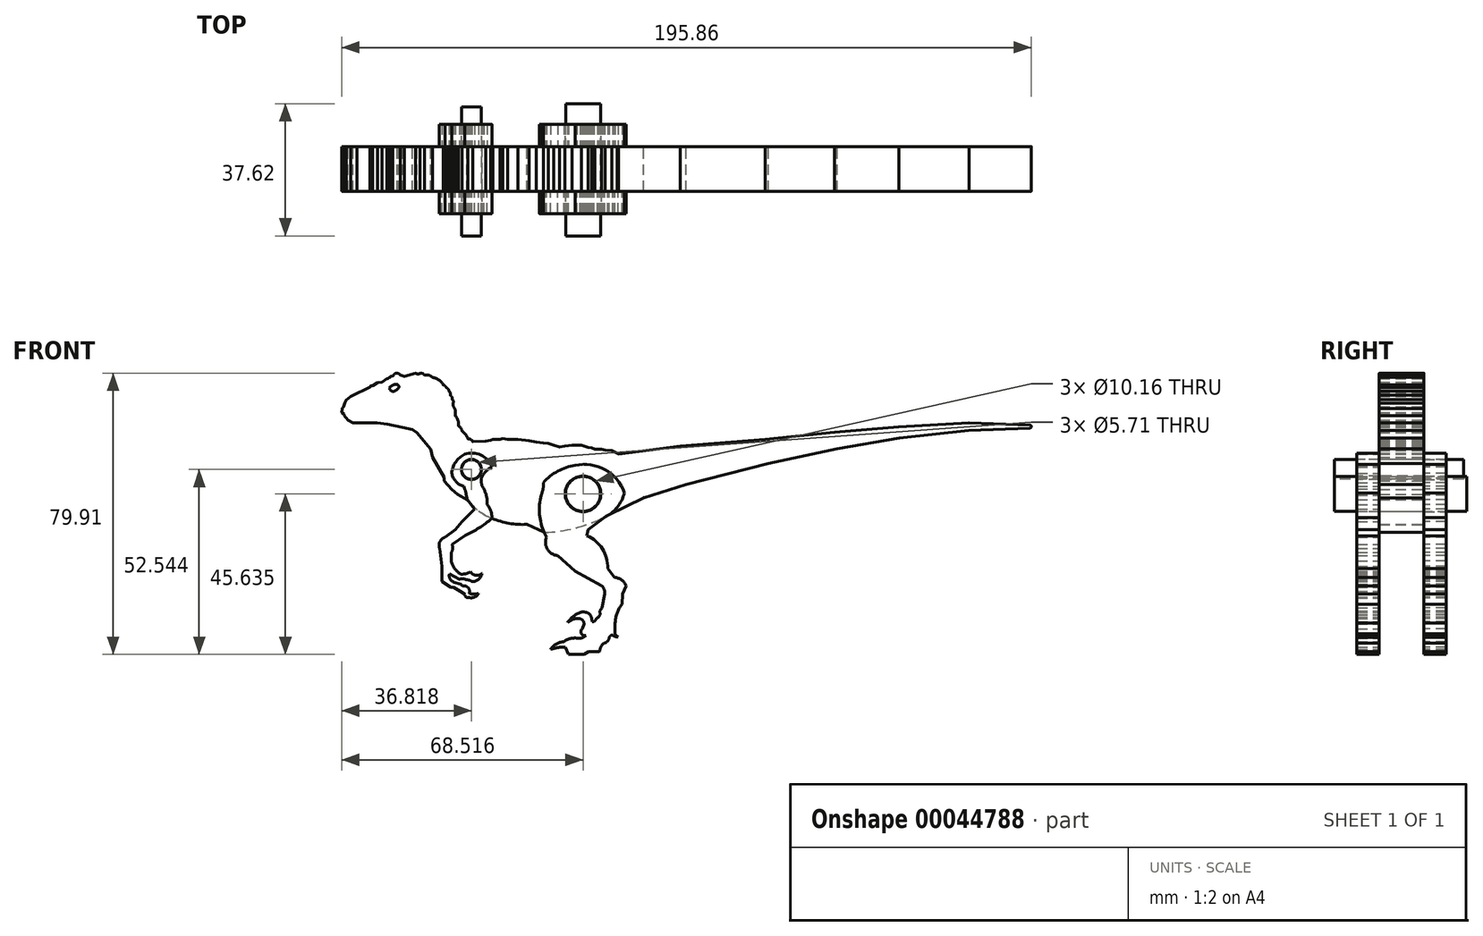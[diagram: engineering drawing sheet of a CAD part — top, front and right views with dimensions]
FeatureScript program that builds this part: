
annotation { "Feature Type Name" : "Feature", "Feature Type Description" : "" }
export const myFeature = defineFeature(function(context is Context, id is Id, definition is map)
    precondition{}
    {
        {
            var Q0;
            Q0=qCreatedBy(makeId("Front.planeOp"),FACE);
            var sketch = newSketch(context, id + "F0", { "sketchPlane" : qUnion([Q0])});
            skLineSegment(sketch, "E0", {"start": v(-125.93, 65.9) * mm, "end": v(-108.35, 68.14) * mm});
            skLineSegment(sketch, "E1", {"start": v(-108.35, 68.14) * mm, "end": v(-84.22, 70.03) * mm});
            skLineSegment(sketch, "E2", {"start": v(-84.22, 70.03) * mm, "end": v(-64.57, 72.1) * mm});
            skLineSegment(sketch, "E3", {"start": v(-64.57, 72.1) * mm, "end": v(-46.3, 73.65) * mm});
            skLineSegment(sketch, "E4", {"start": v(-46.3, 73.65) * mm, "end": v(-26.38, 74.75) * mm});
            skLineSegment(sketch, "E5", {"start": v(-26.38, 74.75) * mm, "end": v(-9.06, 74.08) * mm});
            skArc(sketch, "E6", {"start": v(-9.06, 73.26) * mm, "mid": v(-8.66, 73.67) * mm, "end": v(-9.06, 74.08) * mm});
            skLineSegment(sketch, "E7", {"start": v(-9.06, 73.26) * mm, "end": v(-26.44, 72.6) * mm});
            skLineSegment(sketch, "E8", {"start": v(-26.44, 72.6) * mm, "end": v(-46.15, 70.45) * mm});
            skLineSegment(sketch, "E9", {"start": v(-46.15, 70.45) * mm, "end": v(-63.78, 67.32) * mm});
            skLineSegment(sketch, "E10", {"start": v(-63.78, 67.32) * mm, "end": v(-83.4, 63.22) * mm});
            skLineSegment(sketch, "E11", {"start": v(-83.4, 63.22) * mm, "end": v(-106.71, 57.18) * mm});
            skLineSegment(sketch, "E12", {"start": v(-106.71, 57.18) * mm, "end": v(-118.86, 53.44) * mm});
            skLineSegment(sketch, "E13", {"start": v(-118.86, 53.44) * mm, "end": v(-130.03, 47.9) * mm});
            skPoint(sketch, "E14.endSnap0", {"position": v(-132.94, 9.77) * mm});
            skLineSegment(sketch, "E15", {"start": v(-147.05, 43.57) * mm, "end": v(-151.91, 45.87) * mm});
            skArc(sketch, "E16", {"start": v(-161.96, 47.61) * mm, "mid": v(-157.04, 46.17) * mm, "end": v(-151.91, 45.87) * mm});
            skLineSegment(sketch, "E17", {"start": v(-168.99, 52.93) * mm, "end": v(-171.65, 54.46) * mm});
            skLineSegment(sketch, "E18", {"start": v(-171.65, 54.46) * mm, "end": v(-173.34, 55.8) * mm});
            skLineSegment(sketch, "E19", {"start": v(-173.34, 55.8) * mm, "end": v(-175.45, 58.25) * mm});
            skLineSegment(sketch, "E20", {"start": v(-175.45, 58.25) * mm, "end": v(-175.47, 59.23) * mm});
            skLineSegment(sketch, "E21", {"start": v(-175.47, 59.23) * mm, "end": v(-177.78, 63.2) * mm});
            skLineSegment(sketch, "E22", {"start": v(-177.78, 63.2) * mm, "end": v(-178.8, 64.97) * mm});
            skLineSegment(sketch, "E23", {"start": v(-178.8, 64.97) * mm, "end": v(-179.31, 67.25) * mm});
            skLineSegment(sketch, "E24", {"start": v(-179.31, 67.25) * mm, "end": v(-183.18, 71.9) * mm});
            skLineSegment(sketch, "E25", {"start": v(-183.18, 71.9) * mm, "end": v(-184.49, 72.8) * mm});
            skLineSegment(sketch, "E26", {"start": v(-184.49, 72.8) * mm, "end": v(-187.38, 73.5) * mm});
            skLineSegment(sketch, "E27", {"start": v(-187.38, 73.5) * mm, "end": v(-189.84, 74) * mm});
            skLineSegment(sketch, "E28", {"start": v(-189.84, 74) * mm, "end": v(-191.62, 74.38) * mm});
            skLineSegment(sketch, "E29", {"start": v(-191.62, 74.38) * mm, "end": v(-194.53, 74.67) * mm});
            skLineSegment(sketch, "E30", {"start": v(-194.53, 74.67) * mm, "end": v(-197.25, 74.67) * mm});
            skLineSegment(sketch, "E31", {"start": v(-197.25, 74.67) * mm, "end": v(-200.12, 74.67) * mm});
            skLineSegment(sketch, "E32", {"start": v(-200.12, 74.67) * mm, "end": v(-201.34, 74.67) * mm});
            skLineSegment(sketch, "E33", {"start": v(-201.34, 74.67) * mm, "end": v(-202.78, 75.5) * mm});
            skLineSegment(sketch, "E34", {"start": v(-202.78, 75.5) * mm, "end": v(-203.96, 76.93) * mm});
            skLineSegment(sketch, "E35", {"start": v(-203.96, 77.29) * mm, "end": v(-204.52, 77.65) * mm});
            skLineSegment(sketch, "E36", {"start": v(-204.52, 77.65) * mm, "end": v(-204.44, 78.8) * mm});
            skLineSegment(sketch, "E37", {"start": v(-204.44, 78.8) * mm, "end": v(-204.09, 79.26) * mm});
            skLineSegment(sketch, "E38", {"start": v(-204.09, 79.26) * mm, "end": v(-203.68, 80.39) * mm});
            skLineSegment(sketch, "E39", {"start": v(-203.68, 80.39) * mm, "end": v(-203.32, 81.16) * mm});
            skLineSegment(sketch, "E40", {"start": v(-203.32, 81.16) * mm, "end": v(-201.99, 82.18) * mm});
            skLineSegment(sketch, "E41", {"start": v(-201.99, 82.18) * mm, "end": v(-200.22, 83.1) * mm});
            skLineSegment(sketch, "E42", {"start": v(-200.22, 83.1) * mm, "end": v(-198.01, 84.18) * mm});
            skLineSegment(sketch, "E43", {"start": v(-198.01, 84.18) * mm, "end": v(-196.55, 84.9) * mm});
            skLineSegment(sketch, "E44", {"start": v(-196.55, 84.9) * mm, "end": v(-196.3, 85.25) * mm});
            skLineSegment(sketch, "E45", {"start": v(-196.3, 85.25) * mm, "end": v(-195.76, 85.33) * mm});
            skLineSegment(sketch, "E46", {"start": v(-195.76, 85.33) * mm, "end": v(-194.43, 86.15) * mm});
            skLineSegment(sketch, "E47", {"start": v(-194.43, 86.15) * mm, "end": v(-193.15, 86.23) * mm});
            skLineSegment(sketch, "E48", {"start": v(-193.15, 86.23) * mm, "end": v(-191.76, 87.3) * mm});
            skLineSegment(sketch, "E49", {"start": v(-191.76, 87.3) * mm, "end": v(-191.4, 87.3) * mm});
            skLineSegment(sketch, "E50", {"start": v(-191.4, 87.3) * mm, "end": v(-191, 87.69) * mm});
            skLineSegment(sketch, "E51", {"start": v(-191, 87.69) * mm, "end": v(-190.82, 87.69) * mm});
            skLineSegment(sketch, "E52", {"start": v(-190.82, 87.69) * mm, "end": v(-190.53, 87.94) * mm});
            skLineSegment(sketch, "E53", {"start": v(-190.53, 87.94) * mm, "end": v(-190, 88.02) * mm});
            skArc(sketch, "E54", {"start": v(-187.95, 88.35) * mm, "mid": v(-189.08, 88.84) * mm, "end": v(-190, 88.02) * mm});
            skLineSegment(sketch, "E55", {"start": v(-187.95, 88.35) * mm, "end": v(-186.77, 87.92) * mm});
            skLineSegment(sketch, "E56", {"start": v(-186.77, 87.92) * mm, "end": v(-183.56, 88.85) * mm});
            skArc(sketch, "E57", {"start": v(-183.56, 88.85) * mm, "mid": v(-182.98, 88.62) * mm, "end": v(-182.36, 88.76) * mm});
            skArc(sketch, "E58", {"start": v(-180.98, 88.3) * mm, "mid": v(-181.6, 88.76) * mm, "end": v(-182.36, 88.76) * mm});
            skArc(sketch, "E59", {"start": v(-178.74, 87.64) * mm, "mid": v(-179.77, 88.28) * mm, "end": v(-180.98, 88.3) * mm});
            skArc(sketch, "E60", {"start": v(-175.7, 85.54) * mm, "mid": v(-176.97, 86.96) * mm, "end": v(-178.74, 87.64) * mm});
            skArc(sketch, "E61", {"start": v(-174.82, 84.77) * mm, "mid": v(-175.2, 85.23) * mm, "end": v(-175.7, 85.54) * mm});
            skArc(sketch, "E62", {"start": v(-174.03, 83.74) * mm, "mid": v(-174.33, 84.33) * mm, "end": v(-174.82, 84.77) * mm});
            skArc(sketch, "E63", {"start": v(-173.68, 82.56) * mm, "mid": v(-173.72, 83.2) * mm, "end": v(-174.03, 83.74) * mm});
            skArc(sketch, "E64", {"start": v(-173.11, 81.35) * mm, "mid": v(-173.23, 82.04) * mm, "end": v(-173.68, 82.56) * mm});
            skArc(sketch, "E65", {"start": v(-172.9, 80.34) * mm, "mid": v(-172.83, 80.88) * mm, "end": v(-173.11, 81.35) * mm});
            skArc(sketch, "E66", {"start": v(-172.9, 80.34) * mm, "mid": v(-172.83, 79.49) * mm, "end": v(-172.42, 78.74) * mm});
            skArc(sketch, "E67", {"start": v(-172.28, 76.73) * mm, "mid": v(-172.22, 77.74) * mm, "end": v(-172.42, 78.74) * mm});
            skArc(sketch, "E68", {"start": v(-171.43, 73.91) * mm, "mid": v(-171.52, 75.42) * mm, "end": v(-172.28, 76.73) * mm});
            skArc(sketch, "E69", {"start": v(-170.37, 72.43) * mm, "mid": v(-170.75, 73.28) * mm, "end": v(-171.43, 73.91) * mm});
            skArc(sketch, "E70", {"start": v(-168.66, 70.2) * mm, "mid": v(-169.34, 71.45) * mm, "end": v(-170.37, 72.43) * mm});
            skArc(sketch, "E71", {"start": v(-167.32, 69.36) * mm, "mid": v(-167.86, 69.98) * mm, "end": v(-168.66, 70.2) * mm});
            skLineSegment(sketch, "E72", {"start": v(-167.32, 69.36) * mm, "end": v(-163.58, 69.58) * mm});
            skLineSegment(sketch, "E73", {"start": v(-163.58, 69.58) * mm, "end": v(-162.22, 69.8) * mm});
            skLineSegment(sketch, "E74", {"start": v(-162.22, 69.8) * mm, "end": v(-161.63, 70.06) * mm});
            skLineSegment(sketch, "E75", {"start": v(-161.63, 70.06) * mm, "end": v(-159.56, 70.09) * mm});
            skLineSegment(sketch, "E76", {"start": v(-159.56, 70.09) * mm, "end": v(-158.84, 70.24) * mm});
            skLineSegment(sketch, "E77", {"start": v(-158.84, 70.24) * mm, "end": v(-157.36, 70.06) * mm});
            skLineSegment(sketch, "E78", {"start": v(-157.36, 70.06) * mm, "end": v(-154.44, 70.01) * mm});
            skLineSegment(sketch, "E79", {"start": v(-154.44, 70.01) * mm, "end": v(-151.36, 69.68) * mm});
            skLineSegment(sketch, "E80", {"start": v(-151.36, 69.68) * mm, "end": v(-149.29, 69.27) * mm});
            skLineSegment(sketch, "E81", {"start": v(-149.29, 69.27) * mm, "end": v(-147.29, 69.04) * mm});
            skLineSegment(sketch, "E82", {"start": v(-147.29, 69.04) * mm, "end": v(-145.8, 68.94) * mm});
            skLineSegment(sketch, "E83", {"start": v(-145.8, 68.94) * mm, "end": v(-144.37, 68.37) * mm});
            skLineSegment(sketch, "E84", {"start": v(-144.37, 68.37) * mm, "end": v(-142.63, 67.91) * mm});
            skLineSegment(sketch, "E85", {"start": v(-142.63, 67.91) * mm, "end": v(-141.22, 68.14) * mm});
            skLineSegment(sketch, "E86", {"start": v(-141.22, 68.14) * mm, "end": v(-139.12, 68.32) * mm});
            skLineSegment(sketch, "E87", {"start": v(-139.12, 68.32) * mm, "end": v(-136.45, 68.32) * mm});
            skLineSegment(sketch, "E88", {"start": v(-136.45, 68.32) * mm, "end": v(-134.56, 67.8) * mm});
            skLineSegment(sketch, "E89", {"start": v(-134.56, 67.8) * mm, "end": v(-133.53, 67.68) * mm});
            skLineSegment(sketch, "E90", {"start": v(-133.53, 67.68) * mm, "end": v(-132.64, 67.3) * mm});
            skLineSegment(sketch, "E91", {"start": v(-132.64, 67.3) * mm, "end": v(-130.69, 67.27) * mm});
            skLineSegment(sketch, "E92", {"start": v(-130.69, 67.27) * mm, "end": v(-129.66, 66.99) * mm});
            skLineSegment(sketch, "E93", {"start": v(-129.66, 66.99) * mm, "end": v(-127.82, 66.86) * mm});
            skLineSegment(sketch, "E94", {"start": v(-127.82, 66.86) * mm, "end": v(-126.26, 66.12) * mm});
            skLineSegment(sketch, "E95", {"start": v(-126.26, 66.12) * mm, "end": v(-125.93, 65.9) * mm});
            skArc(sketch, "E96", {"start": v(-188.76, 85.67) * mm, "mid": v(-190.05, 85.46) * mm, "end": v(-191.02, 84.58) * mm});
            skArc(sketch, "E97", {"start": v(-188.28, 84.82) * mm, "mid": v(-188.41, 85.3) * mm, "end": v(-188.76, 85.67) * mm});
            skArc(sketch, "E98", {"start": v(-189.83, 83.66) * mm, "mid": v(-188.94, 84.09) * mm, "end": v(-188.28, 84.82) * mm});
            skArc(sketch, "E99", {"start": v(-191.02, 84.58) * mm, "mid": v(-190.58, 83.92) * mm, "end": v(-189.83, 83.66) * mm});
            skLineSegment(sketch, "E100", {"start": v(-194.53, 74.67) * mm, "end": v(-187.58, 74.67) * mm});
            skArc(sketch, "E101", {"start": v(-187.58, 74.67) * mm, "mid": v(-186.04, 74.88) * mm, "end": v(-184.6, 75.5) * mm});
            skArc(sketch, "E102", {"start": v(-184.6, 75.5) * mm, "mid": v(-183.22, 76.44) * mm, "end": v(-182.32, 77.85) * mm});
            skArc(sketch, "E103", {"start": v(-181.83, 79.96) * mm, "mid": v(-182.4, 78.98) * mm, "end": v(-182.32, 77.85) * mm});
            skLineSegment(sketch, "E104", {"start": v(-203.96, 77.29) * mm, "end": v(-203.96, 76.93) * mm});
            skArc(sketch, "E105", {"start": v(-168.99, 52.93) * mm, "mid": v(-165.8, 49.85) * mm, "end": v(-161.96, 47.61) * mm});
            skPoint(sketch, "E106.end.orphan", {"position": v(-173.5, 37.9) * mm});
            skPoint(sketch, "E107.end.orphan", {"position": v(-165.75, 26.36) * mm});
            skPoint(sketch, "E108.start.orphan", {"position": v(-168.42, 26.36) * mm});
            skPoint(sketch, "E109.center.orphan", {"position": v(-167.5, 32.44) * mm});
            skPoint(sketch, "E110.end.orphan", {"position": v(-168.04, 32.44) * mm});
            skPoint(sketch, "E111.start.orphan", {"position": v(-173.5, 35.58) * mm});
            skArc(sketch, "E112", {"start": v(-147.05, 43.57) * mm, "mid": v(-138.3, 44.84) * mm, "end": v(-130.03, 47.9) * mm});
            skPoint(sketch, "E113.orphan", {"position": v(-131.41, 9.77) * mm});
            skPoint(sketch, "E114.start.orphan", {"position": v(-134.46, 9.77) * mm});
            skPoint(sketch, "E14.end.orphan", {"position": v(-132.94, 18.26) * mm});
            skSolve(sketch);
        }
        {
            var Q0;
            Q0 = qSketchRegion(id + "F0", true);
            extrude(context, id + "F1", {"entities" : qUnion([Q0]), "depth" : 12.7 * mm});
        }
        {
            var Q0;
            Q0=makeQuery(id+"F1.opExtrude","CAP_FACE",FACE,{"disambiguationData":[OSD([sQuery(id+"F0.wireOp",EDGE,"E0"),sQuery(id+"F0.wireOp",EDGE,"E1"),sQuery(id+"F0.wireOp",EDGE,"E2"),sQuery(id+"F0.wireOp",EDGE,"E3"),sQuery(id+"F0.wireOp",EDGE,"E4"),sQuery(id+"F0.wireOp",EDGE,"E5"),sQuery(id+"F0.wireOp",EDGE,"E6"),sQuery(id+"F0.wireOp",EDGE,"E7"),sQuery(id+"F0.wireOp",EDGE,"E8"),sQuery(id+"F0.wireOp",EDGE,"E9"),sQuery(id+"F0.wireOp",EDGE,"E10"),sQuery(id+"F0.wireOp",EDGE,"E11"),sQuery(id+"F0.wireOp",EDGE,"E12"),sQuery(id+"F0.wireOp",EDGE,"E13"),sQuery(id+"F0.wireOp",EDGE,"24e5a3a4-4c74-4cf4-83a0-4dd23b862dd2"),sQuery(id+"F0.wireOp",EDGE,"080116d6-97e3-4202-9e88-d1089f754f1b"),sQuery(id+"F0.wireOp",EDGE,"d3884d33-9078-405f-b6df-4c04f3e83864"),sQuery(id+"F0.wireOp",EDGE,"febd36f7-1211-4430-a0e6-d8187a314ec4"),sQuery(id+"F0.wireOp",EDGE,"da5aa56b-a51a-4f41-be61-5bd352a00608"),sQuery(id+"F0.wireOp",EDGE,"d6cba1f3-012b-44de-a797-d860b0189383"),sQuery(id+"F0.wireOp",EDGE,"37a4c888-297b-4a02-801f-539c14ebc06d"),sQuery(id+"F0.wireOp",EDGE,"e4f4d76b-1661-4bd5-9ee1-3f521e7b8a22"),sQuery(id+"F0.wireOp",EDGE,"979e7fdc-73c7-4f33-a677-fdc23efbcfdc"),sQuery(id+"F0.wireOp",EDGE,"29fca69b-b50e-4ce2-ab5e-5b8caaeedcb0"),sQuery(id+"F0.wireOp",EDGE,"8e0e4076-9d8e-4c43-9cb5-455944ac78b8"),sQuery(id+"F0.wireOp",EDGE,"44bc8136-e123-4d3f-885e-bba49d30737f"),sQuery(id+"F0.wireOp",EDGE,"525c7c83-05e1-4472-ad50-cb793b361226"),sQuery(id+"F0.wireOp",EDGE,"5d251ab0-8bdf-4815-aee8-ee65ace502ef"),sQuery(id+"F0.wireOp",EDGE,"27625abd-22d6-4f79-a906-6ae342303200"),sQuery(id+"F0.wireOp",EDGE,"E114"),sQuery(id+"F0.wireOp",EDGE,"e7f71301-65a4-4f7e-82f1-78113fcac0ca"),sQuery(id+"F0.wireOp",EDGE,"26476aea-994e-4d0f-ac5c-cd76c3ac9e5d"),sQuery(id+"F0.wireOp",EDGE,"03a9189d-c466-419f-af76-e664bc940cea"),sQuery(id+"F0.wireOp",EDGE,"69aa97cf-a6f8-4194-888d-ef945e605e21"),sQuery(id+"F0.wireOp",EDGE,"afc6dbb8-0825-4bc3-9a9d-32ddbc67a7fa"),sQuery(id+"F0.wireOp",EDGE,"0628672f-60e4-485e-babd-115e9d53bd91"),sQuery(id+"F0.wireOp",EDGE,"e0d62bde-7324-42d2-bb55-b3d343f8089d"),sQuery(id+"F0.wireOp",EDGE,"1e4123c9-30b8-4527-b1a6-3343e65eabf4"),sQuery(id+"F0.wireOp",EDGE,"09e39b06-8005-44ff-a5a9-aa5534c9f029"),sQuery(id+"F0.wireOp",EDGE,"23136ab9-187e-40da-8f19-5e2a66e5e931"),sQuery(id+"F0.wireOp",EDGE,"bbcf107a-c80a-4753-81d0-061c0fd05650"),sQuery(id+"F0.wireOp",EDGE,"cf572bc4-ae00-43a8-be20-ca718d7e2706"),sQuery(id+"F0.wireOp",EDGE,"2e92d61d-f502-4e42-9fb1-9756a9c91f70"),sQuery(id+"F0.wireOp",EDGE,"E14"),sQuery(id+"F0.wireOp",EDGE,"ce39f346-d287-4330-8f07-a5cfedcd8c1d"),sQuery(id+"F0.wireOp",EDGE,"58f72196-1935-4dd5-9193-2e0d50fd29e6"),sQuery(id+"F0.wireOp",EDGE,"e48e3e90-8ca5-40ff-9788-39b801b58fd2"),sQuery(id+"F0.wireOp",EDGE,"65447df7-b8a0-446b-9d25-0bb36401ba05"),sQuery(id+"F0.wireOp",EDGE,"5d1346c8-a41c-40e0-b5fa-ddddd0b284a1"),sQuery(id+"F0.wireOp",EDGE,"65ad6121-d8a3-40ab-a185-4ab3d7fadf29"),sQuery(id+"F0.wireOp",EDGE,"d791e0c2-2edb-42dd-ace2-d81078d97bde"),sQuery(id+"F0.wireOp",EDGE,"d9b75e36-ac99-4c51-9c33-fa74f8d5a9b3"),sQuery(id+"F0.wireOp",EDGE,"03808c8b-abac-4ab2-9cbf-64fa338352f3"),sQuery(id+"F0.wireOp",EDGE,"88808034-b678-4790-916c-13f8a42bf5bf"),sQuery(id+"F0.wireOp",EDGE,"87ca94a4-f72d-4e60-8cfd-468d838f297d"),sQuery(id+"F0.wireOp",EDGE,"E15"),sQuery(id+"F0.wireOp",EDGE,"E16"),sQuery(id+"F0.wireOp",EDGE,"56e22c62-bd9a-4330-ac47-cfbe338e8b0b"),sQuery(id+"F0.wireOp",EDGE,"ad8806c6-7dcc-4992-ab26-999b93f7161a"),sQuery(id+"F0.wireOp",EDGE,"04024f97-dbba-4aaf-ac7c-313a9bbd046f"),sQuery(id+"F0.wireOp",EDGE,"de948168-a457-48e4-bb50-c1b5c20a2fc4"),sQuery(id+"F0.wireOp",EDGE,"2bbf0c70-c40e-4de5-9243-abc391f2bf0c"),sQuery(id+"F0.wireOp",EDGE,"be9f5566-fca7-447f-9f60-4b6078c375ac"),sQuery(id+"F0.wireOp",EDGE,"77890933-ceef-4542-9664-65d2eacc818a"),sQuery(id+"F0.wireOp",EDGE,"7c18f7d5-9e43-4cd1-9539-4e8f4f5ca3f1"),sQuery(id+"F0.wireOp",EDGE,"9cc133be-ff1e-47a6-ada5-25dcc5613f2b"),sQuery(id+"F0.wireOp",EDGE,"8dc2e84b-138c-41d1-8304-0eacfba6ff78"),sQuery(id+"F0.wireOp",EDGE,"17c6f588-5742-469e-b3f7-379bf38585fc"),sQuery(id+"F0.wireOp",EDGE,"3fdd379f-cb02-4a36-b395-53968c59bcba"),sQuery(id+"F0.wireOp",EDGE,"f5b93067-485c-4ec9-a1b8-8860950cdd02"),sQuery(id+"F0.wireOp",EDGE,"e42a77d0-4a70-4d4a-ba47-8115e7dc4dcc"),sQuery(id+"F0.wireOp",EDGE,"E107"),sQuery(id+"F0.wireOp",EDGE,"E108"),sQuery(id+"F0.wireOp",EDGE,"8ad39814-4749-4596-98ca-ab9319c44225"),sQuery(id+"F0.wireOp",EDGE,"dbbcd29d-0f3e-4336-8f78-61f0d25b7e47"),sQuery(id+"F0.wireOp",EDGE,"34e004fb-3a68-4636-a58a-67c15d5aa6ee"),sQuery(id+"F0.wireOp",EDGE,"9faae3bd-c1e5-4f2b-ab95-7917c89e5d54"),sQuery(id+"F0.wireOp",EDGE,"8eb61683-85a1-4c01-8b81-4b093b2239ec"),sQuery(id+"F0.wireOp",EDGE,"39f59a45-2d56-49f7-8920-897281f57e23"),sQuery(id+"F0.wireOp",EDGE,"E109"),sQuery(id+"F0.wireOp",EDGE,"31f1a48f-2e70-4db7-b6d9-21c2649d04a3"),sQuery(id+"F0.wireOp",EDGE,"E110"),sQuery(id+"F0.wireOp",EDGE,"E111"),sQuery(id+"F0.wireOp",EDGE,"a0052d91-5333-430d-8703-92b6cdf2263b"),sQuery(id+"F0.wireOp",EDGE,"E106"),sQuery(id+"F0.wireOp",EDGE,"e9ba18ba-eab9-48cb-b754-650d70c20c0d"),sQuery(id+"F0.wireOp",EDGE,"E17"),sQuery(id+"F0.wireOp",EDGE,"E18"),sQuery(id+"F0.wireOp",EDGE,"E19"),sQuery(id+"F0.wireOp",EDGE,"E20"),sQuery(id+"F0.wireOp",EDGE,"E21"),sQuery(id+"F0.wireOp",EDGE,"E22"),sQuery(id+"F0.wireOp",EDGE,"E23"),sQuery(id+"F0.wireOp",EDGE,"E24"),sQuery(id+"F0.wireOp",EDGE,"E25"),sQuery(id+"F0.wireOp",EDGE,"E26"),sQuery(id+"F0.wireOp",EDGE,"E27"),sQuery(id+"F0.wireOp",EDGE,"E28"),sQuery(id+"F0.wireOp",EDGE,"E29"),sQuery(id+"F0.wireOp",EDGE,"E30"),sQuery(id+"F0.wireOp",EDGE,"E31"),sQuery(id+"F0.wireOp",EDGE,"E32"),sQuery(id+"F0.wireOp",EDGE,"E33"),sQuery(id+"F0.wireOp",EDGE,"E34"),sQuery(id+"F0.wireOp",EDGE,"560e0b3a-b859-4922-9c8a-5d52a5039c23"),sQuery(id+"F0.wireOp",EDGE,"E35"),sQuery(id+"F0.wireOp",EDGE,"E36"),sQuery(id+"F0.wireOp",EDGE,"E37"),sQuery(id+"F0.wireOp",EDGE,"E38"),sQuery(id+"F0.wireOp",EDGE,"E39"),sQuery(id+"F0.wireOp",EDGE,"E40"),sQuery(id+"F0.wireOp",EDGE,"E41"),sQuery(id+"F0.wireOp",EDGE,"E42"),sQuery(id+"F0.wireOp",EDGE,"E43"),sQuery(id+"F0.wireOp",EDGE,"E44"),sQuery(id+"F0.wireOp",EDGE,"E45"),sQuery(id+"F0.wireOp",EDGE,"E46"),sQuery(id+"F0.wireOp",EDGE,"E47"),sQuery(id+"F0.wireOp",EDGE,"E48"),sQuery(id+"F0.wireOp",EDGE,"E49"),sQuery(id+"F0.wireOp",EDGE,"E50"),sQuery(id+"F0.wireOp",EDGE,"E51"),sQuery(id+"F0.wireOp",EDGE,"E52"),sQuery(id+"F0.wireOp",EDGE,"E53"),sQuery(id+"F0.wireOp",EDGE,"E54"),sQuery(id+"F0.wireOp",EDGE,"E55"),sQuery(id+"F0.wireOp",EDGE,"E56"),sQuery(id+"F0.wireOp",EDGE,"E57"),sQuery(id+"F0.wireOp",EDGE,"E58"),sQuery(id+"F0.wireOp",EDGE,"E59"),sQuery(id+"F0.wireOp",EDGE,"E60"),sQuery(id+"F0.wireOp",EDGE,"E61"),sQuery(id+"F0.wireOp",EDGE,"E62"),sQuery(id+"F0.wireOp",EDGE,"E63"),sQuery(id+"F0.wireOp",EDGE,"E64"),sQuery(id+"F0.wireOp",EDGE,"E65"),sQuery(id+"F0.wireOp",EDGE,"E66"),sQuery(id+"F0.wireOp",EDGE,"E67"),sQuery(id+"F0.wireOp",EDGE,"E68"),sQuery(id+"F0.wireOp",EDGE,"E69"),sQuery(id+"F0.wireOp",EDGE,"E70"),sQuery(id+"F0.wireOp",EDGE,"E71"),sQuery(id+"F0.wireOp",EDGE,"E72"),sQuery(id+"F0.wireOp",EDGE,"E73"),sQuery(id+"F0.wireOp",EDGE,"E74"),sQuery(id+"F0.wireOp",EDGE,"E75"),sQuery(id+"F0.wireOp",EDGE,"E76"),sQuery(id+"F0.wireOp",EDGE,"E77"),sQuery(id+"F0.wireOp",EDGE,"E78"),sQuery(id+"F0.wireOp",EDGE,"E79"),sQuery(id+"F0.wireOp",EDGE,"E80"),sQuery(id+"F0.wireOp",EDGE,"E81"),sQuery(id+"F0.wireOp",EDGE,"E82"),sQuery(id+"F0.wireOp",EDGE,"E83"),sQuery(id+"F0.wireOp",EDGE,"E84"),sQuery(id+"F0.wireOp",EDGE,"E85"),sQuery(id+"F0.wireOp",EDGE,"E86"),sQuery(id+"F0.wireOp",EDGE,"E87"),sQuery(id+"F0.wireOp",EDGE,"E88"),sQuery(id+"F0.wireOp",EDGE,"E89"),sQuery(id+"F0.wireOp",EDGE,"E90"),sQuery(id+"F0.wireOp",EDGE,"E91"),sQuery(id+"F0.wireOp",EDGE,"E92"),sQuery(id+"F0.wireOp",EDGE,"E93"),sQuery(id+"F0.wireOp",EDGE,"E94"),sQuery(id+"F0.wireOp",EDGE,"E95")])],"isStart":false});
            fillet(context, id + "F2", {"entities" : qUnion([Q0]), "radius" : 0.05 * mm, "tangentPropagation" : true, "allowEdgeOverflow" : false});
        }
        {
            var Q0;
            Q0=makeQuery(id+"F1.opExtrude","CAP_FACE",FACE,{"disambiguationData":[OSD([sQuery(id+"F0.wireOp",EDGE,"E0"),sQuery(id+"F0.wireOp",EDGE,"E1"),sQuery(id+"F0.wireOp",EDGE,"E2"),sQuery(id+"F0.wireOp",EDGE,"E3"),sQuery(id+"F0.wireOp",EDGE,"E4"),sQuery(id+"F0.wireOp",EDGE,"E5"),sQuery(id+"F0.wireOp",EDGE,"E6"),sQuery(id+"F0.wireOp",EDGE,"E7"),sQuery(id+"F0.wireOp",EDGE,"E8"),sQuery(id+"F0.wireOp",EDGE,"E9"),sQuery(id+"F0.wireOp",EDGE,"E10"),sQuery(id+"F0.wireOp",EDGE,"E11"),sQuery(id+"F0.wireOp",EDGE,"E12"),sQuery(id+"F0.wireOp",EDGE,"E13"),sQuery(id+"F0.wireOp",EDGE,"24e5a3a4-4c74-4cf4-83a0-4dd23b862dd2"),sQuery(id+"F0.wireOp",EDGE,"080116d6-97e3-4202-9e88-d1089f754f1b"),sQuery(id+"F0.wireOp",EDGE,"d3884d33-9078-405f-b6df-4c04f3e83864"),sQuery(id+"F0.wireOp",EDGE,"febd36f7-1211-4430-a0e6-d8187a314ec4"),sQuery(id+"F0.wireOp",EDGE,"da5aa56b-a51a-4f41-be61-5bd352a00608"),sQuery(id+"F0.wireOp",EDGE,"d6cba1f3-012b-44de-a797-d860b0189383"),sQuery(id+"F0.wireOp",EDGE,"37a4c888-297b-4a02-801f-539c14ebc06d"),sQuery(id+"F0.wireOp",EDGE,"e4f4d76b-1661-4bd5-9ee1-3f521e7b8a22"),sQuery(id+"F0.wireOp",EDGE,"979e7fdc-73c7-4f33-a677-fdc23efbcfdc"),sQuery(id+"F0.wireOp",EDGE,"29fca69b-b50e-4ce2-ab5e-5b8caaeedcb0"),sQuery(id+"F0.wireOp",EDGE,"8e0e4076-9d8e-4c43-9cb5-455944ac78b8"),sQuery(id+"F0.wireOp",EDGE,"44bc8136-e123-4d3f-885e-bba49d30737f"),sQuery(id+"F0.wireOp",EDGE,"525c7c83-05e1-4472-ad50-cb793b361226"),sQuery(id+"F0.wireOp",EDGE,"5d251ab0-8bdf-4815-aee8-ee65ace502ef"),sQuery(id+"F0.wireOp",EDGE,"27625abd-22d6-4f79-a906-6ae342303200"),sQuery(id+"F0.wireOp",EDGE,"E114"),sQuery(id+"F0.wireOp",EDGE,"e7f71301-65a4-4f7e-82f1-78113fcac0ca"),sQuery(id+"F0.wireOp",EDGE,"26476aea-994e-4d0f-ac5c-cd76c3ac9e5d"),sQuery(id+"F0.wireOp",EDGE,"03a9189d-c466-419f-af76-e664bc940cea"),sQuery(id+"F0.wireOp",EDGE,"69aa97cf-a6f8-4194-888d-ef945e605e21"),sQuery(id+"F0.wireOp",EDGE,"afc6dbb8-0825-4bc3-9a9d-32ddbc67a7fa"),sQuery(id+"F0.wireOp",EDGE,"0628672f-60e4-485e-babd-115e9d53bd91"),sQuery(id+"F0.wireOp",EDGE,"e0d62bde-7324-42d2-bb55-b3d343f8089d"),sQuery(id+"F0.wireOp",EDGE,"1e4123c9-30b8-4527-b1a6-3343e65eabf4"),sQuery(id+"F0.wireOp",EDGE,"09e39b06-8005-44ff-a5a9-aa5534c9f029"),sQuery(id+"F0.wireOp",EDGE,"23136ab9-187e-40da-8f19-5e2a66e5e931"),sQuery(id+"F0.wireOp",EDGE,"bbcf107a-c80a-4753-81d0-061c0fd05650"),sQuery(id+"F0.wireOp",EDGE,"cf572bc4-ae00-43a8-be20-ca718d7e2706"),sQuery(id+"F0.wireOp",EDGE,"2e92d61d-f502-4e42-9fb1-9756a9c91f70"),sQuery(id+"F0.wireOp",EDGE,"E14"),sQuery(id+"F0.wireOp",EDGE,"ce39f346-d287-4330-8f07-a5cfedcd8c1d"),sQuery(id+"F0.wireOp",EDGE,"58f72196-1935-4dd5-9193-2e0d50fd29e6"),sQuery(id+"F0.wireOp",EDGE,"e48e3e90-8ca5-40ff-9788-39b801b58fd2"),sQuery(id+"F0.wireOp",EDGE,"65447df7-b8a0-446b-9d25-0bb36401ba05"),sQuery(id+"F0.wireOp",EDGE,"5d1346c8-a41c-40e0-b5fa-ddddd0b284a1"),sQuery(id+"F0.wireOp",EDGE,"65ad6121-d8a3-40ab-a185-4ab3d7fadf29"),sQuery(id+"F0.wireOp",EDGE,"d791e0c2-2edb-42dd-ace2-d81078d97bde"),sQuery(id+"F0.wireOp",EDGE,"d9b75e36-ac99-4c51-9c33-fa74f8d5a9b3"),sQuery(id+"F0.wireOp",EDGE,"03808c8b-abac-4ab2-9cbf-64fa338352f3"),sQuery(id+"F0.wireOp",EDGE,"88808034-b678-4790-916c-13f8a42bf5bf"),sQuery(id+"F0.wireOp",EDGE,"87ca94a4-f72d-4e60-8cfd-468d838f297d"),sQuery(id+"F0.wireOp",EDGE,"E15"),sQuery(id+"F0.wireOp",EDGE,"E16"),sQuery(id+"F0.wireOp",EDGE,"56e22c62-bd9a-4330-ac47-cfbe338e8b0b"),sQuery(id+"F0.wireOp",EDGE,"ad8806c6-7dcc-4992-ab26-999b93f7161a"),sQuery(id+"F0.wireOp",EDGE,"04024f97-dbba-4aaf-ac7c-313a9bbd046f"),sQuery(id+"F0.wireOp",EDGE,"de948168-a457-48e4-bb50-c1b5c20a2fc4"),sQuery(id+"F0.wireOp",EDGE,"2bbf0c70-c40e-4de5-9243-abc391f2bf0c"),sQuery(id+"F0.wireOp",EDGE,"be9f5566-fca7-447f-9f60-4b6078c375ac"),sQuery(id+"F0.wireOp",EDGE,"77890933-ceef-4542-9664-65d2eacc818a"),sQuery(id+"F0.wireOp",EDGE,"7c18f7d5-9e43-4cd1-9539-4e8f4f5ca3f1"),sQuery(id+"F0.wireOp",EDGE,"9cc133be-ff1e-47a6-ada5-25dcc5613f2b"),sQuery(id+"F0.wireOp",EDGE,"8dc2e84b-138c-41d1-8304-0eacfba6ff78"),sQuery(id+"F0.wireOp",EDGE,"17c6f588-5742-469e-b3f7-379bf38585fc"),sQuery(id+"F0.wireOp",EDGE,"3fdd379f-cb02-4a36-b395-53968c59bcba"),sQuery(id+"F0.wireOp",EDGE,"f5b93067-485c-4ec9-a1b8-8860950cdd02"),sQuery(id+"F0.wireOp",EDGE,"e42a77d0-4a70-4d4a-ba47-8115e7dc4dcc"),sQuery(id+"F0.wireOp",EDGE,"E107"),sQuery(id+"F0.wireOp",EDGE,"E108"),sQuery(id+"F0.wireOp",EDGE,"8ad39814-4749-4596-98ca-ab9319c44225"),sQuery(id+"F0.wireOp",EDGE,"dbbcd29d-0f3e-4336-8f78-61f0d25b7e47"),sQuery(id+"F0.wireOp",EDGE,"34e004fb-3a68-4636-a58a-67c15d5aa6ee"),sQuery(id+"F0.wireOp",EDGE,"9faae3bd-c1e5-4f2b-ab95-7917c89e5d54"),sQuery(id+"F0.wireOp",EDGE,"8eb61683-85a1-4c01-8b81-4b093b2239ec"),sQuery(id+"F0.wireOp",EDGE,"39f59a45-2d56-49f7-8920-897281f57e23"),sQuery(id+"F0.wireOp",EDGE,"E109"),sQuery(id+"F0.wireOp",EDGE,"31f1a48f-2e70-4db7-b6d9-21c2649d04a3"),sQuery(id+"F0.wireOp",EDGE,"E110"),sQuery(id+"F0.wireOp",EDGE,"E111"),sQuery(id+"F0.wireOp",EDGE,"a0052d91-5333-430d-8703-92b6cdf2263b"),sQuery(id+"F0.wireOp",EDGE,"E106"),sQuery(id+"F0.wireOp",EDGE,"e9ba18ba-eab9-48cb-b754-650d70c20c0d"),sQuery(id+"F0.wireOp",EDGE,"E17"),sQuery(id+"F0.wireOp",EDGE,"E18"),sQuery(id+"F0.wireOp",EDGE,"E19"),sQuery(id+"F0.wireOp",EDGE,"E20"),sQuery(id+"F0.wireOp",EDGE,"E21"),sQuery(id+"F0.wireOp",EDGE,"E22"),sQuery(id+"F0.wireOp",EDGE,"E23"),sQuery(id+"F0.wireOp",EDGE,"E24"),sQuery(id+"F0.wireOp",EDGE,"E25"),sQuery(id+"F0.wireOp",EDGE,"E26"),sQuery(id+"F0.wireOp",EDGE,"E27"),sQuery(id+"F0.wireOp",EDGE,"E28"),sQuery(id+"F0.wireOp",EDGE,"E29"),sQuery(id+"F0.wireOp",EDGE,"E30"),sQuery(id+"F0.wireOp",EDGE,"E31"),sQuery(id+"F0.wireOp",EDGE,"E32"),sQuery(id+"F0.wireOp",EDGE,"E33"),sQuery(id+"F0.wireOp",EDGE,"E34"),sQuery(id+"F0.wireOp",EDGE,"E35"),sQuery(id+"F0.wireOp",EDGE,"E36"),sQuery(id+"F0.wireOp",EDGE,"E37"),sQuery(id+"F0.wireOp",EDGE,"E38"),sQuery(id+"F0.wireOp",EDGE,"E39"),sQuery(id+"F0.wireOp",EDGE,"E40"),sQuery(id+"F0.wireOp",EDGE,"E41"),sQuery(id+"F0.wireOp",EDGE,"E42"),sQuery(id+"F0.wireOp",EDGE,"E43"),sQuery(id+"F0.wireOp",EDGE,"E44"),sQuery(id+"F0.wireOp",EDGE,"E45"),sQuery(id+"F0.wireOp",EDGE,"E46"),sQuery(id+"F0.wireOp",EDGE,"E47"),sQuery(id+"F0.wireOp",EDGE,"E48"),sQuery(id+"F0.wireOp",EDGE,"E49"),sQuery(id+"F0.wireOp",EDGE,"E50"),sQuery(id+"F0.wireOp",EDGE,"E51"),sQuery(id+"F0.wireOp",EDGE,"E52"),sQuery(id+"F0.wireOp",EDGE,"E53"),sQuery(id+"F0.wireOp",EDGE,"E54"),sQuery(id+"F0.wireOp",EDGE,"E55"),sQuery(id+"F0.wireOp",EDGE,"E56"),sQuery(id+"F0.wireOp",EDGE,"E57"),sQuery(id+"F0.wireOp",EDGE,"E58"),sQuery(id+"F0.wireOp",EDGE,"E59"),sQuery(id+"F0.wireOp",EDGE,"E60"),sQuery(id+"F0.wireOp",EDGE,"E61"),sQuery(id+"F0.wireOp",EDGE,"E62"),sQuery(id+"F0.wireOp",EDGE,"E63"),sQuery(id+"F0.wireOp",EDGE,"E64"),sQuery(id+"F0.wireOp",EDGE,"E65"),sQuery(id+"F0.wireOp",EDGE,"E66"),sQuery(id+"F0.wireOp",EDGE,"E67"),sQuery(id+"F0.wireOp",EDGE,"E68"),sQuery(id+"F0.wireOp",EDGE,"E69"),sQuery(id+"F0.wireOp",EDGE,"E70"),sQuery(id+"F0.wireOp",EDGE,"E71"),sQuery(id+"F0.wireOp",EDGE,"E72"),sQuery(id+"F0.wireOp",EDGE,"E73"),sQuery(id+"F0.wireOp",EDGE,"E74"),sQuery(id+"F0.wireOp",EDGE,"E75"),sQuery(id+"F0.wireOp",EDGE,"E76"),sQuery(id+"F0.wireOp",EDGE,"E77"),sQuery(id+"F0.wireOp",EDGE,"E78"),sQuery(id+"F0.wireOp",EDGE,"E79"),sQuery(id+"F0.wireOp",EDGE,"E80"),sQuery(id+"F0.wireOp",EDGE,"E81"),sQuery(id+"F0.wireOp",EDGE,"E82"),sQuery(id+"F0.wireOp",EDGE,"E83"),sQuery(id+"F0.wireOp",EDGE,"E84"),sQuery(id+"F0.wireOp",EDGE,"E85"),sQuery(id+"F0.wireOp",EDGE,"E86"),sQuery(id+"F0.wireOp",EDGE,"E87"),sQuery(id+"F0.wireOp",EDGE,"E88"),sQuery(id+"F0.wireOp",EDGE,"E89"),sQuery(id+"F0.wireOp",EDGE,"E90"),sQuery(id+"F0.wireOp",EDGE,"E91"),sQuery(id+"F0.wireOp",EDGE,"E92"),sQuery(id+"F0.wireOp",EDGE,"E93"),sQuery(id+"F0.wireOp",EDGE,"E94"),sQuery(id+"F0.wireOp",EDGE,"E95"),sQuery(id+"F0.wireOp",EDGE,"E96"),sQuery(id+"F0.wireOp",EDGE,"E97"),sQuery(id+"F0.wireOp",EDGE,"E98"),sQuery(id+"F0.wireOp",EDGE,"E99"),sQuery(id+"F0.wireOp",EDGE,"E104")])],"isStart":false});
            var sketch = newSketch(context, id + "F3", { "sketchPlane" : qUnion([Q0])});
            skLineSegment(sketch, "E115", {"start": v(25.76, -7.02) * mm, "end": v(21.18, -10.45) * mm});
            skLineSegment(sketch, "E116", {"start": v(21.18, -10.45) * mm, "end": v(20.82, -12.22) * mm});
            skArc(sketch, "E117", {"start": v(26.71, -21.5) * mm, "mid": v(25.2, -15.94) * mm, "end": v(20.82, -12.22) * mm});
            skLineSegment(sketch, "E118", {"start": v(26.71, -21.5) * mm, "end": v(28.63, -24.06) * mm});
            skArc(sketch, "E119", {"start": v(31.94, -26.54) * mm, "mid": v(30.67, -24.79) * mm, "end": v(28.63, -24.06) * mm});
            skLineSegment(sketch, "E120", {"start": v(31.94, -26.54) * mm, "end": v(30.96, -28.8) * mm});
            skLineSegment(sketch, "E121", {"start": v(30.96, -28.8) * mm, "end": v(30.73, -31.69) * mm});
            skArc(sketch, "E122", {"start": v(30.73, -31.69) * mm, "mid": v(29.37, -34.2) * mm, "end": v(28.81, -37.02) * mm});
            skLineSegment(sketch, "E123", {"start": v(28.81, -37.02) * mm, "end": v(28.81, -40.12) * mm});
            skArc(sketch, "E124", {"start": v(28.81, -40.12) * mm, "mid": v(29.15, -40.6) * mm, "end": v(29.66, -40.91) * mm});
            skArc(sketch, "E125", {"start": v(28.08, -40.4) * mm, "mid": v(28.8, -40.87) * mm, "end": v(29.66, -40.91) * mm});
            skArc(sketch, "E126", {"start": v(28.08, -40.4) * mm, "mid": v(27.51, -40.63) * mm, "end": v(27.13, -41.11) * mm});
            skArc(sketch, "E127", {"start": v(25.55, -42.79) * mm, "mid": v(26.65, -42.24) * mm, "end": v(27.13, -41.11) * mm});
            skArc(sketch, "E128", {"start": v(25.55, -42.79) * mm, "mid": v(24.76, -43.87) * mm, "end": v(24.37, -45.15) * mm});
            skLineSegment(sketch, "E129", {"start": v(24.37, -45.15) * mm, "end": v(21.32, -45.15) * mm});
            skLineSegment(sketch, "E130", {"start": v(21.32, -45.15) * mm, "end": v(20.03, -45.92) * mm});
            skLineSegment(sketch, "E131", {"start": v(20.03, -45.92) * mm, "end": v(15.61, -45.92) * mm});
            skArc(sketch, "E132", {"start": v(18.03, -41.33) * mm, "mid": v(19.38, -41.26) * mm, "end": v(20.52, -40.54) * mm});
            skArc(sketch, "E133", {"start": v(18.03, -41.33) * mm, "mid": v(16.06, -41.44) * mm, "end": v(14.3, -42.33) * mm});
            skArc(sketch, "E134", {"start": v(14.3, -42.33) * mm, "mid": v(12.13, -43) * mm, "end": v(10.46, -44.54) * mm});
            skArc(sketch, "E135", {"start": v(14.64, -43.94) * mm, "mid": v(12.52, -44.01) * mm, "end": v(10.46, -44.54) * mm});
            skLineSegment(sketch, "E136", {"start": v(14.64, -43.94) * mm, "end": v(15.61, -45.92) * mm});
            skArc(sketch, "E137", {"start": v(19.51, -38.62) * mm, "mid": v(19.2, -40.01) * mm, "end": v(20.52, -40.54) * mm});
            skArc(sketch, "E138", {"start": v(18.97, -33.97) * mm, "mid": v(16.92, -35.17) * mm, "end": v(15.31, -36.94) * mm});
            skArc(sketch, "E139", {"start": v(21.8, -34.76) * mm, "mid": v(20.5, -33.98) * mm, "end": v(18.97, -33.97) * mm});
            skArc(sketch, "E140", {"start": v(22.25, -36.66) * mm, "mid": v(22.14, -35.68) * mm, "end": v(21.8, -34.76) * mm});
            skArc(sketch, "E141", {"start": v(18.89, -35.82) * mm, "mid": v(16.96, -35.94) * mm, "end": v(15.31, -36.94) * mm});
            skArc(sketch, "E142", {"start": v(19.96, -37.3) * mm, "mid": v(19.69, -36.37) * mm, "end": v(18.89, -35.82) * mm});
            skLineSegment(sketch, "E143", {"start": v(19.96, -37.3) * mm, "end": v(19.51, -38.62) * mm});
            skLineSegment(sketch, "E144", {"start": v(22.25, -36.66) * mm, "end": v(22.85, -36.66) * mm});
            skPoint(sketch, "E144.endSnap0", {"position": v(22.85, -45.15) * mm});
            skLineSegment(sketch, "E145", {"start": v(22.85, -36.66) * mm, "end": v(23.81, -35.5) * mm});
            skLineSegment(sketch, "E146", {"start": v(23.81, -35.5) * mm, "end": v(24.1, -35.39) * mm});
            skLineSegment(sketch, "E147", {"start": v(24.1, -35.39) * mm, "end": v(24.54, -34.67) * mm});
            skLineSegment(sketch, "E148", {"start": v(24.54, -34.67) * mm, "end": v(24.43, -33.54) * mm});
            skLineSegment(sketch, "E149", {"start": v(24.43, -33.54) * mm, "end": v(25.04, -32.74) * mm});
            skLineSegment(sketch, "E150", {"start": v(25.04, -32.74) * mm, "end": v(25.8, -28.72) * mm});
            skArc(sketch, "E151", {"start": v(25.8, -28.72) * mm, "mid": v(25.67, -27.37) * mm, "end": v(24.83, -26.3) * mm});
            skLineSegment(sketch, "E152", {"start": v(24.83, -26.3) * mm, "end": v(17.47, -22.24) * mm});
            skLineSegment(sketch, "E153", {"start": v(17.47, -22.24) * mm, "end": v(12.47, -17.85) * mm});
            skArc(sketch, "E154", {"start": v(9.32, -12.6) * mm, "mid": v(9.57, -16.02) * mm, "end": v(12.47, -17.85) * mm});
            skLineSegment(sketch, "E155", {"start": v(9.32, -12.6) * mm, "end": v(8.74, -11.35) * mm});
            skArc(sketch, "E156", {"start": v(-13.8, -12.12) * mm, "mid": v(-9.82, -9.98) * mm, "end": v(-6.17, -7.3) * mm});
            skLineSegment(sketch, "E157", {"start": v(-13.8, -12.12) * mm, "end": v(-17.5, -14.63) * mm});
            skLineSegment(sketch, "E158", {"start": v(-11.09, -4.59) * mm, "end": v(-14.68, -8.18) * mm});
            skLineSegment(sketch, "E159", {"start": v(-14.68, -8.18) * mm, "end": v(-16.62, -10.43) * mm});
            skLineSegment(sketch, "E160", {"start": v(-16.62, -10.43) * mm, "end": v(-19.44, -12.63) * mm});
            skArc(sketch, "E161", {"start": v(-19.44, -12.63) * mm, "mid": v(-20.95, -13.86) * mm, "end": v(-21.04, -15.8) * mm});
            skLineSegment(sketch, "E162", {"start": v(-21.04, -15.8) * mm, "end": v(-20.4, -20.89) * mm});
            skLineSegment(sketch, "E163", {"start": v(-20.4, -20.89) * mm, "end": v(-20.4, -25.15) * mm});
            skLineSegment(sketch, "E164", {"start": v(-20.4, -25.15) * mm, "end": v(-17.8, -26.92) * mm});
            skLineSegment(sketch, "E165", {"start": v(-17.8, -26.92) * mm, "end": v(-17.12, -26.92) * mm});
            skLineSegment(sketch, "E166", {"start": v(-17.12, -26.92) * mm, "end": v(-15.14, -28) * mm});
            skLineSegment(sketch, "E167", {"start": v(-15.14, -28) * mm, "end": v(-13.84, -28.95) * mm});
            skArc(sketch, "E168", {"start": v(-13.84, -28.95) * mm, "mid": v(-13.57, -29.62) * mm, "end": v(-12.85, -29.72) * mm});
            skArc(sketch, "E169", {"start": v(-12.85, -29.72) * mm, "mid": v(-11.18, -29.7) * mm, "end": v(-9.97, -28.56) * mm});
            skArc(sketch, "E170", {"start": v(-12.64, -28.56) * mm, "mid": v(-11.3, -28.84) * mm, "end": v(-9.97, -28.56) * mm});
            skArc(sketch, "E171", {"start": v(-12.64, -28.56) * mm, "mid": v(-12.96, -26.96) * mm, "end": v(-14.53, -26.53) * mm});
            skLineSegment(sketch, "E172", {"start": v(-14.53, -26.53) * mm, "end": v(-15, -26.02) * mm});
            skLineSegment(sketch, "E173", {"start": v(-15, -26.02) * mm, "end": v(-16.94, -25.41) * mm});
            skArc(sketch, "E174", {"start": v(-18.24, -23) * mm, "mid": v(-18.09, -24.47) * mm, "end": v(-16.94, -25.41) * mm});
            skLineSegment(sketch, "E175", {"start": v(-18.24, -23) * mm, "end": v(-15.4, -24.6) * mm});
            skArc(sketch, "E176", {"start": v(-13.5, -24.77) * mm, "mid": v(-14.42, -24.42) * mm, "end": v(-15.4, -24.6) * mm});
            skArc(sketch, "E177", {"start": v(-11.86, -25.24) * mm, "mid": v(-12.64, -24.85) * mm, "end": v(-13.5, -24.77) * mm});
            skArc(sketch, "E178", {"start": v(-11.86, -25.24) * mm, "mid": v(-9.96, -24.62) * mm, "end": v(-8.97, -22.87) * mm});
            skArc(sketch, "E179", {"start": v(-12.25, -22.48) * mm, "mid": v(-10.7, -23.46) * mm, "end": v(-8.97, -22.87) * mm});
            skArc(sketch, "E180", {"start": v(-15, -23.13) * mm, "mid": v(-13.58, -23) * mm, "end": v(-12.25, -22.48) * mm});
            skArc(sketch, "E181", {"start": v(-17.72, -19.34) * mm, "mid": v(-16.8, -21.55) * mm, "end": v(-15, -23.13) * mm});
            skArc(sketch, "E182", {"start": v(-17.72, -17.01) * mm, "mid": v(-17.34, -15.85) * mm, "end": v(-17.5, -14.63) * mm});
            skLineSegment(sketch, "E183", {"start": v(-17.72, -19.34) * mm, "end": v(-17.72, -17.01) * mm});
            skLineSegment(sketch, "E184", {"start": v(-11.09, -4.59) * mm, "end": v(-13.2, -2) * mm});
            skArc(sketch, "E185", {"start": v(-17.58, 5.57) * mm, "mid": v(-16.42, 3.2) * mm, "end": v(-14.17, 1.8) * mm});
            skArc(sketch, "E186", {"start": v(-13.2, -2) * mm, "mid": v(-13.58, -0.07) * mm, "end": v(-14.17, 1.8) * mm});
            skArc(sketch, "E187", {"start": v(-6.19, 7.34) * mm, "mid": v(-7.97, 6) * mm, "end": v(-9.24, 4.17) * mm});
            skArc(sketch, "E188", {"start": v(-9.24, 4.17) * mm, "mid": v(-9.13, 2.59) * mm, "end": v(-8.5, 1.12) * mm});
            skArc(sketch, "E189", {"start": v(-7.53, -3.38) * mm, "mid": v(-7.7, -1.06) * mm, "end": v(-8.5, 1.12) * mm});
            skArc(sketch, "E190", {"start": v(-6.17, -7.3) * mm, "mid": v(-6.5, -5.22) * mm, "end": v(-7.53, -3.38) * mm});
            skArc(sketch, "E191", {"start": v(-13.93, 10.93) * mm, "mid": v(-16.48, 8.75) * mm, "end": v(-17.58, 5.57) * mm});
            skArc(sketch, "E192", {"start": v(25.76, -7.02) * mm, "mid": v(29.37, -4.14) * mm, "end": v(31.46, -0.03) * mm});
            skArc(sketch, "E193", {"start": v(7.82, -0.7) * mm, "mid": v(7.34, -6.1) * mm, "end": v(8.74, -11.35) * mm});
            skArc(sketch, "E194", {"start": v(7.82, -0.7) * mm, "mid": v(8.33, 1.06) * mm, "end": v(8.43, 2.9) * mm});
            skArc(sketch, "E195", {"start": v(17.45, 7.77) * mm, "mid": v(12.5, 6.13) * mm, "end": v(8.43, 2.9) * mm});
            skArc(sketch, "E196", {"start": v(31.46, -0.03) * mm, "mid": v(25.95, 6.54) * mm, "end": v(17.45, 7.77) * mm});
            skArc(sketch, "E197", {"start": v(-6.19, 7.34) * mm, "mid": v(-9.33, 10.7) * mm, "end": v(-13.93, 10.93) * mm});
            skPoint(sketch, "E198.end.orphan", {"position": v(146.73, 19.16) * mm});
            skPoint(sketch, "E198.start.orphan", {"position": v(146.73, 18.35) * mm});
            skPoint(sketch, "E199.end.orphan", {"position": v(-48.73, 22.73) * mm});
            skSolve(sketch);
        }
        {
            var Q0;
            Q0=makeQuery(id+"F3.imprint","IMPRINT",FACE,{"disambiguationData":[TD([[makeQuery(id+"F3.imprint","IMPRINT",EDGE,{"derivedFrom":sQuery(id+"F3.wireOp",EDGE,"E115")}),-1.0]])]});
            var Q1;
            Q1=makeQuery(id+"F3.imprint","IMPRINT",FACE,{"disambiguationData":[TD([[makeQuery(id+"F3.imprint","IMPRINT",EDGE,{"derivedFrom":sQuery(id+"F3.wireOp",EDGE,"E156")}),1.0]])]});
            extrude(context, id + "F4", {"entities" : qUnion([Q0, Q1]), "depth" : 6.35 * mm});
        }
        {
            var Q0;
            Q0=makeQuery(id+"F4.opExtrude","SWEPT_BODY",BODY,{"disambiguationData":[OSD([sQuery(id+"F3.wireOp",EDGE,"E115"),sQuery(id+"F3.wireOp",EDGE,"E116"),sQuery(id+"F3.wireOp",EDGE,"E117"),sQuery(id+"F3.wireOp",EDGE,"E118"),sQuery(id+"F3.wireOp",EDGE,"E119"),sQuery(id+"F3.wireOp",EDGE,"E120"),sQuery(id+"F3.wireOp",EDGE,"E121"),sQuery(id+"F3.wireOp",EDGE,"E122"),sQuery(id+"F3.wireOp",EDGE,"E123"),sQuery(id+"F3.wireOp",EDGE,"E124"),sQuery(id+"F3.wireOp",EDGE,"E125"),sQuery(id+"F3.wireOp",EDGE,"E126"),sQuery(id+"F3.wireOp",EDGE,"E127"),sQuery(id+"F3.wireOp",EDGE,"E128"),sQuery(id+"F3.wireOp",EDGE,"E129"),sQuery(id+"F3.wireOp",EDGE,"E130"),sQuery(id+"F3.wireOp",EDGE,"E131"),sQuery(id+"F3.wireOp",EDGE,"E132"),sQuery(id+"F3.wireOp",EDGE,"E133"),sQuery(id+"F3.wireOp",EDGE,"E134"),sQuery(id+"F3.wireOp",EDGE,"E135"),sQuery(id+"F3.wireOp",EDGE,"E136"),sQuery(id+"F3.wireOp",EDGE,"E137"),sQuery(id+"F3.wireOp",EDGE,"E138"),sQuery(id+"F3.wireOp",EDGE,"E139"),sQuery(id+"F3.wireOp",EDGE,"E140"),sQuery(id+"F3.wireOp",EDGE,"E141"),sQuery(id+"F3.wireOp",EDGE,"E142"),sQuery(id+"F3.wireOp",EDGE,"E143"),sQuery(id+"F3.wireOp",EDGE,"E144"),sQuery(id+"F3.wireOp",EDGE,"E145"),sQuery(id+"F3.wireOp",EDGE,"E146"),sQuery(id+"F3.wireOp",EDGE,"E147"),sQuery(id+"F3.wireOp",EDGE,"E148"),sQuery(id+"F3.wireOp",EDGE,"E149"),sQuery(id+"F3.wireOp",EDGE,"E150"),sQuery(id+"F3.wireOp",EDGE,"E151"),sQuery(id+"F3.wireOp",EDGE,"E152"),sQuery(id+"F3.wireOp",EDGE,"E153"),sQuery(id+"F3.wireOp",EDGE,"E154"),sQuery(id+"F3.wireOp",EDGE,"E155"),sQuery(id+"F3.wireOp",EDGE,"E192"),sQuery(id+"F3.wireOp",EDGE,"E193"),sQuery(id+"F3.wireOp",EDGE,"E194"),sQuery(id+"F3.wireOp",EDGE,"E195"),sQuery(id+"F3.wireOp",EDGE,"E196")])]});
            var Q1;
            Q1=makeQuery(id+"F4.opExtrude","SWEPT_BODY",BODY,{"disambiguationData":[OSD([sQuery(id+"F3.wireOp",EDGE,"E156"),sQuery(id+"F3.wireOp",EDGE,"E157"),sQuery(id+"F3.wireOp",EDGE,"E158"),sQuery(id+"F3.wireOp",EDGE,"E159"),sQuery(id+"F3.wireOp",EDGE,"E160"),sQuery(id+"F3.wireOp",EDGE,"E161"),sQuery(id+"F3.wireOp",EDGE,"E162"),sQuery(id+"F3.wireOp",EDGE,"E163"),sQuery(id+"F3.wireOp",EDGE,"E164"),sQuery(id+"F3.wireOp",EDGE,"E165"),sQuery(id+"F3.wireOp",EDGE,"E166"),sQuery(id+"F3.wireOp",EDGE,"E167"),sQuery(id+"F3.wireOp",EDGE,"E168"),sQuery(id+"F3.wireOp",EDGE,"E169"),sQuery(id+"F3.wireOp",EDGE,"E170"),sQuery(id+"F3.wireOp",EDGE,"E171"),sQuery(id+"F3.wireOp",EDGE,"E172"),sQuery(id+"F3.wireOp",EDGE,"E173"),sQuery(id+"F3.wireOp",EDGE,"E174"),sQuery(id+"F3.wireOp",EDGE,"E175"),sQuery(id+"F3.wireOp",EDGE,"E176"),sQuery(id+"F3.wireOp",EDGE,"E177"),sQuery(id+"F3.wireOp",EDGE,"E178"),sQuery(id+"F3.wireOp",EDGE,"E179"),sQuery(id+"F3.wireOp",EDGE,"E180"),sQuery(id+"F3.wireOp",EDGE,"E181"),sQuery(id+"F3.wireOp",EDGE,"E182"),sQuery(id+"F3.wireOp",EDGE,"E183"),sQuery(id+"F3.wireOp",EDGE,"E184"),sQuery(id+"F3.wireOp",EDGE,"E185"),sQuery(id+"F3.wireOp",EDGE,"E186"),sQuery(id+"F3.wireOp",EDGE,"E187"),sQuery(id+"F3.wireOp",EDGE,"E188"),sQuery(id+"F3.wireOp",EDGE,"E189"),sQuery(id+"F3.wireOp",EDGE,"E190"),sQuery(id+"F3.wireOp",EDGE,"E191"),sQuery(id+"F3.wireOp",EDGE,"E197")])]});
            transform(context, id + "F5", {"entities" : qUnion([Q0, Q1]), "transformType" : TransformType.TRANSLATION_3D, "dx" : -155.7 * mm, "dy" : 0 * mm, "dz" : 54.86 * mm, "makeCopy" : false});
        }
        {
            var Q0;
            Q0=makeQuery(id+"F1.opExtrude","CAP_FACE",FACE,{"disambiguationData":[OSD([sQuery(id+"F0.wireOp",EDGE,"E0"),sQuery(id+"F0.wireOp",EDGE,"E1"),sQuery(id+"F0.wireOp",EDGE,"E2"),sQuery(id+"F0.wireOp",EDGE,"E3"),sQuery(id+"F0.wireOp",EDGE,"E4"),sQuery(id+"F0.wireOp",EDGE,"E5"),sQuery(id+"F0.wireOp",EDGE,"E6"),sQuery(id+"F0.wireOp",EDGE,"E7"),sQuery(id+"F0.wireOp",EDGE,"E8"),sQuery(id+"F0.wireOp",EDGE,"E9"),sQuery(id+"F0.wireOp",EDGE,"E10"),sQuery(id+"F0.wireOp",EDGE,"E11"),sQuery(id+"F0.wireOp",EDGE,"E12"),sQuery(id+"F0.wireOp",EDGE,"E13"),sQuery(id+"F0.wireOp",EDGE,"E15"),sQuery(id+"F0.wireOp",EDGE,"E16"),sQuery(id+"F0.wireOp",EDGE,"E17"),sQuery(id+"F0.wireOp",EDGE,"E18"),sQuery(id+"F0.wireOp",EDGE,"E19"),sQuery(id+"F0.wireOp",EDGE,"E20"),sQuery(id+"F0.wireOp",EDGE,"E21"),sQuery(id+"F0.wireOp",EDGE,"E22"),sQuery(id+"F0.wireOp",EDGE,"E23"),sQuery(id+"F0.wireOp",EDGE,"E24"),sQuery(id+"F0.wireOp",EDGE,"E25"),sQuery(id+"F0.wireOp",EDGE,"E26"),sQuery(id+"F0.wireOp",EDGE,"E27"),sQuery(id+"F0.wireOp",EDGE,"E28"),sQuery(id+"F0.wireOp",EDGE,"E29"),sQuery(id+"F0.wireOp",EDGE,"E30"),sQuery(id+"F0.wireOp",EDGE,"E31"),sQuery(id+"F0.wireOp",EDGE,"E32"),sQuery(id+"F0.wireOp",EDGE,"E33"),sQuery(id+"F0.wireOp",EDGE,"E34"),sQuery(id+"F0.wireOp",EDGE,"E35"),sQuery(id+"F0.wireOp",EDGE,"E36"),sQuery(id+"F0.wireOp",EDGE,"E37"),sQuery(id+"F0.wireOp",EDGE,"E38"),sQuery(id+"F0.wireOp",EDGE,"E39"),sQuery(id+"F0.wireOp",EDGE,"E40"),sQuery(id+"F0.wireOp",EDGE,"E41"),sQuery(id+"F0.wireOp",EDGE,"E42"),sQuery(id+"F0.wireOp",EDGE,"E43"),sQuery(id+"F0.wireOp",EDGE,"E44"),sQuery(id+"F0.wireOp",EDGE,"E45"),sQuery(id+"F0.wireOp",EDGE,"E46"),sQuery(id+"F0.wireOp",EDGE,"E47"),sQuery(id+"F0.wireOp",EDGE,"E48"),sQuery(id+"F0.wireOp",EDGE,"E49"),sQuery(id+"F0.wireOp",EDGE,"E50"),sQuery(id+"F0.wireOp",EDGE,"E51"),sQuery(id+"F0.wireOp",EDGE,"E52"),sQuery(id+"F0.wireOp",EDGE,"E53"),sQuery(id+"F0.wireOp",EDGE,"E54"),sQuery(id+"F0.wireOp",EDGE,"E55"),sQuery(id+"F0.wireOp",EDGE,"E56"),sQuery(id+"F0.wireOp",EDGE,"E57"),sQuery(id+"F0.wireOp",EDGE,"E58"),sQuery(id+"F0.wireOp",EDGE,"E59"),sQuery(id+"F0.wireOp",EDGE,"E60"),sQuery(id+"F0.wireOp",EDGE,"E61"),sQuery(id+"F0.wireOp",EDGE,"E62"),sQuery(id+"F0.wireOp",EDGE,"E63"),sQuery(id+"F0.wireOp",EDGE,"E64"),sQuery(id+"F0.wireOp",EDGE,"E65"),sQuery(id+"F0.wireOp",EDGE,"E66"),sQuery(id+"F0.wireOp",EDGE,"E67"),sQuery(id+"F0.wireOp",EDGE,"E68"),sQuery(id+"F0.wireOp",EDGE,"E69"),sQuery(id+"F0.wireOp",EDGE,"E70"),sQuery(id+"F0.wireOp",EDGE,"E71"),sQuery(id+"F0.wireOp",EDGE,"E72"),sQuery(id+"F0.wireOp",EDGE,"E73"),sQuery(id+"F0.wireOp",EDGE,"E74"),sQuery(id+"F0.wireOp",EDGE,"E75"),sQuery(id+"F0.wireOp",EDGE,"E76"),sQuery(id+"F0.wireOp",EDGE,"E77"),sQuery(id+"F0.wireOp",EDGE,"E78"),sQuery(id+"F0.wireOp",EDGE,"E79"),sQuery(id+"F0.wireOp",EDGE,"E80"),sQuery(id+"F0.wireOp",EDGE,"E81"),sQuery(id+"F0.wireOp",EDGE,"E82"),sQuery(id+"F0.wireOp",EDGE,"E83"),sQuery(id+"F0.wireOp",EDGE,"E84"),sQuery(id+"F0.wireOp",EDGE,"E85"),sQuery(id+"F0.wireOp",EDGE,"E86"),sQuery(id+"F0.wireOp",EDGE,"E87"),sQuery(id+"F0.wireOp",EDGE,"E88"),sQuery(id+"F0.wireOp",EDGE,"E89"),sQuery(id+"F0.wireOp",EDGE,"E90"),sQuery(id+"F0.wireOp",EDGE,"E91"),sQuery(id+"F0.wireOp",EDGE,"E92"),sQuery(id+"F0.wireOp",EDGE,"E93"),sQuery(id+"F0.wireOp",EDGE,"E94"),sQuery(id+"F0.wireOp",EDGE,"E95"),sQuery(id+"F0.wireOp",EDGE,"E96"),sQuery(id+"F0.wireOp",EDGE,"E97"),sQuery(id+"F0.wireOp",EDGE,"E98"),sQuery(id+"F0.wireOp",EDGE,"E99"),sQuery(id+"F0.wireOp",EDGE,"E104"),sQuery(id+"F0.wireOp",EDGE,"E105"),sQuery(id+"F0.wireOp",EDGE,"E112")])],"isStart":false});
            var sketch = newSketch(context, id + "F6", { "sketchPlane" : qUnion([Q0])});
            skCircle(sketch, "E200", {"center": v(-167.7, 61.48) * mm, "radius": 2.86 * mm});
            skCircle(sketch, "E201", {"center": v(-136, 54.57) * mm, "radius": 5.08 * mm});
            skLineSegment(sketch, "E202", {"start": v(-141.08, 54.55) * mm, "end": v(-130.92, 54.55) * mm});
            skLineSegment(sketch, "E203", {"start": v(-136, 54.57) * mm, "end": v(-136, 49.5) * mm});
            skLineSegment(sketch, "E204", {"start": v(-136, 49.5) * mm, "end": v(-136, 54.57) * mm});
            skLineSegment(sketch, "E205", {"start": v(-136, 54.57) * mm, "end": v(-136, 59.65) * mm});
            skLineSegment(sketch, "E206", {"start": v(-167.7, 61.48) * mm, "end": v(-166.83, 64.2) * mm});
            skLineSegment(sketch, "E207", {"start": v(-167.7, 61.48) * mm, "end": v(-168.57, 58.76) * mm});
            skLineSegment(sketch, "E208", {"start": v(-168.57, 58.76) * mm, "end": v(-167.7, 61.48) * mm});
            skLineSegment(sketch, "E209", {"start": v(-167.7, 61.48) * mm, "end": v(-164.98, 60.61) * mm});
            skLineSegment(sketch, "E210", {"start": v(-167.7, 61.48) * mm, "end": v(-170.42, 62.35) * mm});
            skSolve(sketch);
        }
        {
            var Q0;
            Q0 = qSketchRegion(id + "F6", true);
            extrude(context, id + "F7", {"entities" : qUnion([Q0]), "operationType" : NewBodyOperationType.REMOVE, "oppositeDirection" : true, "depth" : 25.4 * mm, "hasSecondDirection" : true, "secondDirectionOppositeDirection" : false, "secondDirectionDepth" : 25.4 * mm});
        }
        {
            var Q0;
            Q0=makeQuery(id+"F4.opExtrude","CAP_FACE",FACE,{"disambiguationData":[OSD([sQuery(id+"F3.wireOp",EDGE,"E115"),sQuery(id+"F3.wireOp",EDGE,"E116"),sQuery(id+"F3.wireOp",EDGE,"E117"),sQuery(id+"F3.wireOp",EDGE,"E118"),sQuery(id+"F3.wireOp",EDGE,"E119"),sQuery(id+"F3.wireOp",EDGE,"E120"),sQuery(id+"F3.wireOp",EDGE,"E121"),sQuery(id+"F3.wireOp",EDGE,"E122"),sQuery(id+"F3.wireOp",EDGE,"E123"),sQuery(id+"F3.wireOp",EDGE,"E124"),sQuery(id+"F3.wireOp",EDGE,"E125"),sQuery(id+"F3.wireOp",EDGE,"E126"),sQuery(id+"F3.wireOp",EDGE,"E127"),sQuery(id+"F3.wireOp",EDGE,"E128"),sQuery(id+"F3.wireOp",EDGE,"E129"),sQuery(id+"F3.wireOp",EDGE,"E130"),sQuery(id+"F3.wireOp",EDGE,"E131"),sQuery(id+"F3.wireOp",EDGE,"E132"),sQuery(id+"F3.wireOp",EDGE,"E133"),sQuery(id+"F3.wireOp",EDGE,"E134"),sQuery(id+"F3.wireOp",EDGE,"E135"),sQuery(id+"F3.wireOp",EDGE,"E136"),sQuery(id+"F3.wireOp",EDGE,"E137"),sQuery(id+"F3.wireOp",EDGE,"E138"),sQuery(id+"F3.wireOp",EDGE,"E139"),sQuery(id+"F3.wireOp",EDGE,"E140"),sQuery(id+"F3.wireOp",EDGE,"E141"),sQuery(id+"F3.wireOp",EDGE,"E142"),sQuery(id+"F3.wireOp",EDGE,"E143"),sQuery(id+"F3.wireOp",EDGE,"E144"),sQuery(id+"F3.wireOp",EDGE,"E145"),sQuery(id+"F3.wireOp",EDGE,"E146"),sQuery(id+"F3.wireOp",EDGE,"E147"),sQuery(id+"F3.wireOp",EDGE,"E148"),sQuery(id+"F3.wireOp",EDGE,"E149"),sQuery(id+"F3.wireOp",EDGE,"E150"),sQuery(id+"F3.wireOp",EDGE,"E151"),sQuery(id+"F3.wireOp",EDGE,"E152"),sQuery(id+"F3.wireOp",EDGE,"E153"),sQuery(id+"F3.wireOp",EDGE,"E154"),sQuery(id+"F3.wireOp",EDGE,"E155"),sQuery(id+"F3.wireOp",EDGE,"E192"),sQuery(id+"F3.wireOp",EDGE,"E193"),sQuery(id+"F3.wireOp",EDGE,"E194"),sQuery(id+"F3.wireOp",EDGE,"E195"),sQuery(id+"F3.wireOp",EDGE,"E196")])],"isStart":false});
            var sketch = newSketch(context, id + "F8", { "sketchPlane" : qUnion([Q0])});
            skPoint(sketch, "E211.first.point", {"position": v(-138.42, 50.1) * mm});
            skPoint(sketch, "E211.second.point", {"position": v(-131.05, 55.71) * mm});
            skPoint(sketch, "E211.third.point", {"position": v(-139.43, 58.32) * mm});
            skCircle(sketch, "E212", {"center": v(-136, 54.57) * mm, "radius": 4.95 * mm});
            skSolve(sketch);
        }
        {
            var Q0;
            Q0 = qSketchRegion(id + "F8", true);
            extrude(context, id + "F9", {"entities" : qUnion([Q0]), "depth" : 6.35 * mm, "hasSecondDirection" : true, "secondDirectionOppositeDirection" : true, "secondDirectionDepth" : 31.27 * mm});
        }
        {
            var Q0;
            Q0=makeQuery(id+"F4.opExtrude","CAP_FACE",FACE,{"disambiguationData":[OSD([sQuery(id+"F3.wireOp",EDGE,"E156"),sQuery(id+"F3.wireOp",EDGE,"E157"),sQuery(id+"F3.wireOp",EDGE,"E158"),sQuery(id+"F3.wireOp",EDGE,"E159"),sQuery(id+"F3.wireOp",EDGE,"E160"),sQuery(id+"F3.wireOp",EDGE,"E161"),sQuery(id+"F3.wireOp",EDGE,"E162"),sQuery(id+"F3.wireOp",EDGE,"E163"),sQuery(id+"F3.wireOp",EDGE,"E164"),sQuery(id+"F3.wireOp",EDGE,"E165"),sQuery(id+"F3.wireOp",EDGE,"E166"),sQuery(id+"F3.wireOp",EDGE,"E167"),sQuery(id+"F3.wireOp",EDGE,"E168"),sQuery(id+"F3.wireOp",EDGE,"E169"),sQuery(id+"F3.wireOp",EDGE,"E170"),sQuery(id+"F3.wireOp",EDGE,"E171"),sQuery(id+"F3.wireOp",EDGE,"E172"),sQuery(id+"F3.wireOp",EDGE,"E173"),sQuery(id+"F3.wireOp",EDGE,"E174"),sQuery(id+"F3.wireOp",EDGE,"E175"),sQuery(id+"F3.wireOp",EDGE,"E176"),sQuery(id+"F3.wireOp",EDGE,"E177"),sQuery(id+"F3.wireOp",EDGE,"E178"),sQuery(id+"F3.wireOp",EDGE,"E179"),sQuery(id+"F3.wireOp",EDGE,"E180"),sQuery(id+"F3.wireOp",EDGE,"E181"),sQuery(id+"F3.wireOp",EDGE,"E182"),sQuery(id+"F3.wireOp",EDGE,"E183"),sQuery(id+"F3.wireOp",EDGE,"E184"),sQuery(id+"F3.wireOp",EDGE,"E185"),sQuery(id+"F3.wireOp",EDGE,"E186"),sQuery(id+"F3.wireOp",EDGE,"E187"),sQuery(id+"F3.wireOp",EDGE,"E188"),sQuery(id+"F3.wireOp",EDGE,"E189"),sQuery(id+"F3.wireOp",EDGE,"E190"),sQuery(id+"F3.wireOp",EDGE,"E191"),sQuery(id+"F3.wireOp",EDGE,"E197")])],"isStart":false});
            var sketch = newSketch(context, id + "F10", { "sketchPlane" : qUnion([Q0])});
            skPoint(sketch, "E213.first.point", {"position": v(-169.94, 59.71) * mm});
            skPoint(sketch, "E213.second.point", {"position": v(-164.85, 61.59) * mm});
            skPoint(sketch, "E213.third.point", {"position": v(-168.8, 64.12) * mm});
            skCircle(sketch, "E214", {"center": v(-167.7, 61.48) * mm, "radius": 2.8 * mm});
            skSolve(sketch);
        }
        {
            var Q0;
            Q0 = qSketchRegion(id + "F10", true);
            extrude(context, id + "F11", {"entities" : qUnion([Q0]), "depth" : 6.35 * mm, "hasDraft" : true, "draftAngle" : 0 * degree, "hasSecondDirection" : true, "secondDirectionOppositeDirection" : true, "secondDirectionDepth" : 30.36 * mm});
        }
        {
            var Q0;
            Q0=makeQuery(id+"F1.opExtrude","CAP_FACE",FACE,{"disambiguationData":[OSD([sQuery(id+"F0.wireOp",EDGE,"E0"),sQuery(id+"F0.wireOp",EDGE,"E1"),sQuery(id+"F0.wireOp",EDGE,"E2"),sQuery(id+"F0.wireOp",EDGE,"E3"),sQuery(id+"F0.wireOp",EDGE,"E4"),sQuery(id+"F0.wireOp",EDGE,"E5"),sQuery(id+"F0.wireOp",EDGE,"E6"),sQuery(id+"F0.wireOp",EDGE,"E7"),sQuery(id+"F0.wireOp",EDGE,"E8"),sQuery(id+"F0.wireOp",EDGE,"E9"),sQuery(id+"F0.wireOp",EDGE,"E10"),sQuery(id+"F0.wireOp",EDGE,"E11"),sQuery(id+"F0.wireOp",EDGE,"E12"),sQuery(id+"F0.wireOp",EDGE,"E13"),sQuery(id+"F0.wireOp",EDGE,"E15"),sQuery(id+"F0.wireOp",EDGE,"E16"),sQuery(id+"F0.wireOp",EDGE,"E17"),sQuery(id+"F0.wireOp",EDGE,"E18"),sQuery(id+"F0.wireOp",EDGE,"E19"),sQuery(id+"F0.wireOp",EDGE,"E20"),sQuery(id+"F0.wireOp",EDGE,"E21"),sQuery(id+"F0.wireOp",EDGE,"E22"),sQuery(id+"F0.wireOp",EDGE,"E23"),sQuery(id+"F0.wireOp",EDGE,"E24"),sQuery(id+"F0.wireOp",EDGE,"E25"),sQuery(id+"F0.wireOp",EDGE,"E26"),sQuery(id+"F0.wireOp",EDGE,"E27"),sQuery(id+"F0.wireOp",EDGE,"E28"),sQuery(id+"F0.wireOp",EDGE,"E29"),sQuery(id+"F0.wireOp",EDGE,"E30"),sQuery(id+"F0.wireOp",EDGE,"E31"),sQuery(id+"F0.wireOp",EDGE,"E32"),sQuery(id+"F0.wireOp",EDGE,"E33"),sQuery(id+"F0.wireOp",EDGE,"E34"),sQuery(id+"F0.wireOp",EDGE,"E35"),sQuery(id+"F0.wireOp",EDGE,"E36"),sQuery(id+"F0.wireOp",EDGE,"E37"),sQuery(id+"F0.wireOp",EDGE,"E38"),sQuery(id+"F0.wireOp",EDGE,"E39"),sQuery(id+"F0.wireOp",EDGE,"E40"),sQuery(id+"F0.wireOp",EDGE,"E41"),sQuery(id+"F0.wireOp",EDGE,"E42"),sQuery(id+"F0.wireOp",EDGE,"E43"),sQuery(id+"F0.wireOp",EDGE,"E44"),sQuery(id+"F0.wireOp",EDGE,"E45"),sQuery(id+"F0.wireOp",EDGE,"E46"),sQuery(id+"F0.wireOp",EDGE,"E47"),sQuery(id+"F0.wireOp",EDGE,"E48"),sQuery(id+"F0.wireOp",EDGE,"E49"),sQuery(id+"F0.wireOp",EDGE,"E50"),sQuery(id+"F0.wireOp",EDGE,"E51"),sQuery(id+"F0.wireOp",EDGE,"E52"),sQuery(id+"F0.wireOp",EDGE,"E53"),sQuery(id+"F0.wireOp",EDGE,"E54"),sQuery(id+"F0.wireOp",EDGE,"E55"),sQuery(id+"F0.wireOp",EDGE,"E56"),sQuery(id+"F0.wireOp",EDGE,"E57"),sQuery(id+"F0.wireOp",EDGE,"E58"),sQuery(id+"F0.wireOp",EDGE,"E59"),sQuery(id+"F0.wireOp",EDGE,"E60"),sQuery(id+"F0.wireOp",EDGE,"E61"),sQuery(id+"F0.wireOp",EDGE,"E62"),sQuery(id+"F0.wireOp",EDGE,"E63"),sQuery(id+"F0.wireOp",EDGE,"E64"),sQuery(id+"F0.wireOp",EDGE,"E65"),sQuery(id+"F0.wireOp",EDGE,"E66"),sQuery(id+"F0.wireOp",EDGE,"E67"),sQuery(id+"F0.wireOp",EDGE,"E68"),sQuery(id+"F0.wireOp",EDGE,"E69"),sQuery(id+"F0.wireOp",EDGE,"E70"),sQuery(id+"F0.wireOp",EDGE,"E71"),sQuery(id+"F0.wireOp",EDGE,"E72"),sQuery(id+"F0.wireOp",EDGE,"E73"),sQuery(id+"F0.wireOp",EDGE,"E74"),sQuery(id+"F0.wireOp",EDGE,"E75"),sQuery(id+"F0.wireOp",EDGE,"E76"),sQuery(id+"F0.wireOp",EDGE,"E77"),sQuery(id+"F0.wireOp",EDGE,"E78"),sQuery(id+"F0.wireOp",EDGE,"E79"),sQuery(id+"F0.wireOp",EDGE,"E80"),sQuery(id+"F0.wireOp",EDGE,"E81"),sQuery(id+"F0.wireOp",EDGE,"E82"),sQuery(id+"F0.wireOp",EDGE,"E83"),sQuery(id+"F0.wireOp",EDGE,"E84"),sQuery(id+"F0.wireOp",EDGE,"E85"),sQuery(id+"F0.wireOp",EDGE,"E86"),sQuery(id+"F0.wireOp",EDGE,"E87"),sQuery(id+"F0.wireOp",EDGE,"E88"),sQuery(id+"F0.wireOp",EDGE,"E89"),sQuery(id+"F0.wireOp",EDGE,"E90"),sQuery(id+"F0.wireOp",EDGE,"E91"),sQuery(id+"F0.wireOp",EDGE,"E92"),sQuery(id+"F0.wireOp",EDGE,"E93"),sQuery(id+"F0.wireOp",EDGE,"E94"),sQuery(id+"F0.wireOp",EDGE,"E95"),sQuery(id+"F0.wireOp",EDGE,"E96"),sQuery(id+"F0.wireOp",EDGE,"E97"),sQuery(id+"F0.wireOp",EDGE,"E98"),sQuery(id+"F0.wireOp",EDGE,"E99"),sQuery(id+"F0.wireOp",EDGE,"E104"),sQuery(id+"F0.wireOp",EDGE,"E105"),sQuery(id+"F0.wireOp",EDGE,"E112")])],"isStart":false});
            cPlane(context, id + "F12", {"entities" : qUnion([Q0]), "cplaneType" : CPlaneType.OFFSET, "offset" : 6.35 * mm, "oppositeDirection" : true, "width" : 152.4 * mm, "height" : 152.4 * mm});
        }
        {
            var Q0;
            Q0=makeQuery(id+"F4.opExtrude","SWEPT_BODY",BODY,{"disambiguationData":[OSD([sQuery(id+"F3.wireOp",EDGE,"E115"),sQuery(id+"F3.wireOp",EDGE,"E116"),sQuery(id+"F3.wireOp",EDGE,"E117"),sQuery(id+"F3.wireOp",EDGE,"E118"),sQuery(id+"F3.wireOp",EDGE,"E119"),sQuery(id+"F3.wireOp",EDGE,"E120"),sQuery(id+"F3.wireOp",EDGE,"E121"),sQuery(id+"F3.wireOp",EDGE,"E122"),sQuery(id+"F3.wireOp",EDGE,"E123"),sQuery(id+"F3.wireOp",EDGE,"E124"),sQuery(id+"F3.wireOp",EDGE,"E125"),sQuery(id+"F3.wireOp",EDGE,"E126"),sQuery(id+"F3.wireOp",EDGE,"E127"),sQuery(id+"F3.wireOp",EDGE,"E128"),sQuery(id+"F3.wireOp",EDGE,"E129"),sQuery(id+"F3.wireOp",EDGE,"E130"),sQuery(id+"F3.wireOp",EDGE,"E131"),sQuery(id+"F3.wireOp",EDGE,"E132"),sQuery(id+"F3.wireOp",EDGE,"E133"),sQuery(id+"F3.wireOp",EDGE,"E134"),sQuery(id+"F3.wireOp",EDGE,"E135"),sQuery(id+"F3.wireOp",EDGE,"E136"),sQuery(id+"F3.wireOp",EDGE,"E137"),sQuery(id+"F3.wireOp",EDGE,"E138"),sQuery(id+"F3.wireOp",EDGE,"E139"),sQuery(id+"F3.wireOp",EDGE,"E140"),sQuery(id+"F3.wireOp",EDGE,"E141"),sQuery(id+"F3.wireOp",EDGE,"E142"),sQuery(id+"F3.wireOp",EDGE,"E143"),sQuery(id+"F3.wireOp",EDGE,"E144"),sQuery(id+"F3.wireOp",EDGE,"E145"),sQuery(id+"F3.wireOp",EDGE,"E146"),sQuery(id+"F3.wireOp",EDGE,"E147"),sQuery(id+"F3.wireOp",EDGE,"E148"),sQuery(id+"F3.wireOp",EDGE,"E149"),sQuery(id+"F3.wireOp",EDGE,"E150"),sQuery(id+"F3.wireOp",EDGE,"E151"),sQuery(id+"F3.wireOp",EDGE,"E152"),sQuery(id+"F3.wireOp",EDGE,"E153"),sQuery(id+"F3.wireOp",EDGE,"E154"),sQuery(id+"F3.wireOp",EDGE,"E155"),sQuery(id+"F3.wireOp",EDGE,"E192"),sQuery(id+"F3.wireOp",EDGE,"E193"),sQuery(id+"F3.wireOp",EDGE,"E194"),sQuery(id+"F3.wireOp",EDGE,"E195"),sQuery(id+"F3.wireOp",EDGE,"E196")])]});
            var Q1;
            Q1=makeQuery(id+"F4.opExtrude","SWEPT_BODY",BODY,{"disambiguationData":[OSD([sQuery(id+"F3.wireOp",EDGE,"E156"),sQuery(id+"F3.wireOp",EDGE,"E157"),sQuery(id+"F3.wireOp",EDGE,"E158"),sQuery(id+"F3.wireOp",EDGE,"E159"),sQuery(id+"F3.wireOp",EDGE,"E160"),sQuery(id+"F3.wireOp",EDGE,"E161"),sQuery(id+"F3.wireOp",EDGE,"E162"),sQuery(id+"F3.wireOp",EDGE,"E163"),sQuery(id+"F3.wireOp",EDGE,"E164"),sQuery(id+"F3.wireOp",EDGE,"E165"),sQuery(id+"F3.wireOp",EDGE,"E166"),sQuery(id+"F3.wireOp",EDGE,"E167"),sQuery(id+"F3.wireOp",EDGE,"E168"),sQuery(id+"F3.wireOp",EDGE,"E169"),sQuery(id+"F3.wireOp",EDGE,"E170"),sQuery(id+"F3.wireOp",EDGE,"E171"),sQuery(id+"F3.wireOp",EDGE,"E172"),sQuery(id+"F3.wireOp",EDGE,"E173"),sQuery(id+"F3.wireOp",EDGE,"E174"),sQuery(id+"F3.wireOp",EDGE,"E175"),sQuery(id+"F3.wireOp",EDGE,"E176"),sQuery(id+"F3.wireOp",EDGE,"E177"),sQuery(id+"F3.wireOp",EDGE,"E178"),sQuery(id+"F3.wireOp",EDGE,"E179"),sQuery(id+"F3.wireOp",EDGE,"E180"),sQuery(id+"F3.wireOp",EDGE,"E181"),sQuery(id+"F3.wireOp",EDGE,"E182"),sQuery(id+"F3.wireOp",EDGE,"E183"),sQuery(id+"F3.wireOp",EDGE,"E184"),sQuery(id+"F3.wireOp",EDGE,"E185"),sQuery(id+"F3.wireOp",EDGE,"E186"),sQuery(id+"F3.wireOp",EDGE,"E187"),sQuery(id+"F3.wireOp",EDGE,"E188"),sQuery(id+"F3.wireOp",EDGE,"E189"),sQuery(id+"F3.wireOp",EDGE,"E190"),sQuery(id+"F3.wireOp",EDGE,"E191"),sQuery(id+"F3.wireOp",EDGE,"E197")])]});
            var Q2;
            Q2=qCreatedBy(id+"F12.planeOp",FACE);
            mirror(context, id + "F13", {"entities" : qUnion([Q0, Q1]), "mirrorPlane" : qUnion([Q2])});
        }
    });
